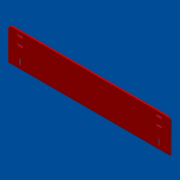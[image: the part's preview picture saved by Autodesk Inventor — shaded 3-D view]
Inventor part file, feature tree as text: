
AUTODESK INVENTOR PART (.ipt)
format: ipt  version: 2012 SP1 (Build 160190100, 190)  size: 122,880 bytes
history: native  units: in
note: dims shown in document units (in); Inventor stores cm internally (conversion verified against a paired STEP export)
features: extrude x3, sketch x3, pattern_linear x2, fillet x1
ambient origin geometry x8: Origin, YZ Plane, XZ Plane, XY Plane, X Axis, Y Axis, Z Axis, Center Point
bodies: Solid1 (feature_tree)
feature tree (9):
  extrude  "Extrusion1"  Depth=15.748in
  extrude  "Extrusion2"  Depth=0.1969in
  pattern_linear  "Rectangular Pattern1"  Spacing1=0.3937in  [1 undecoded]
  fillet  "Fillet1"  Radius=0.1969in
  extrude  "Extrusion3"  Depth=0.3937in
  pattern_linear  "Rectangular Pattern2"  Spacing1=0.1345in  [1 undecoded]
  sketch  "Sketch1"  dims[d0=3.1496in d1=15.748in]
  sketch  "Sketch2"  dims[d2=0.1345in d3=0.0in d4=0.1969in d6=0.3937in]
  sketch  "Sketch3"  dims[d7=0.1969in d8=0.3937in d9=0.1969in d10=0.3937in d13=0.1345in d14=0.0in d15=0.7874in d17=13.4724in d18=0.7874in d20=0.7874in d21=0.3937in d22=0.1969in d23=0.1969in d24=0.3937in d25=0.3937in d26=1.1378in d27=1.1378in d28=0.1345in d29=0.0in d30=0.7874in d32=13.4724in]
note: 2 required parameter values undecoded (feature->parameter linkage not recoverable at this tier; creation-order binding heuristic only, values carry confidence <= 0.55)
